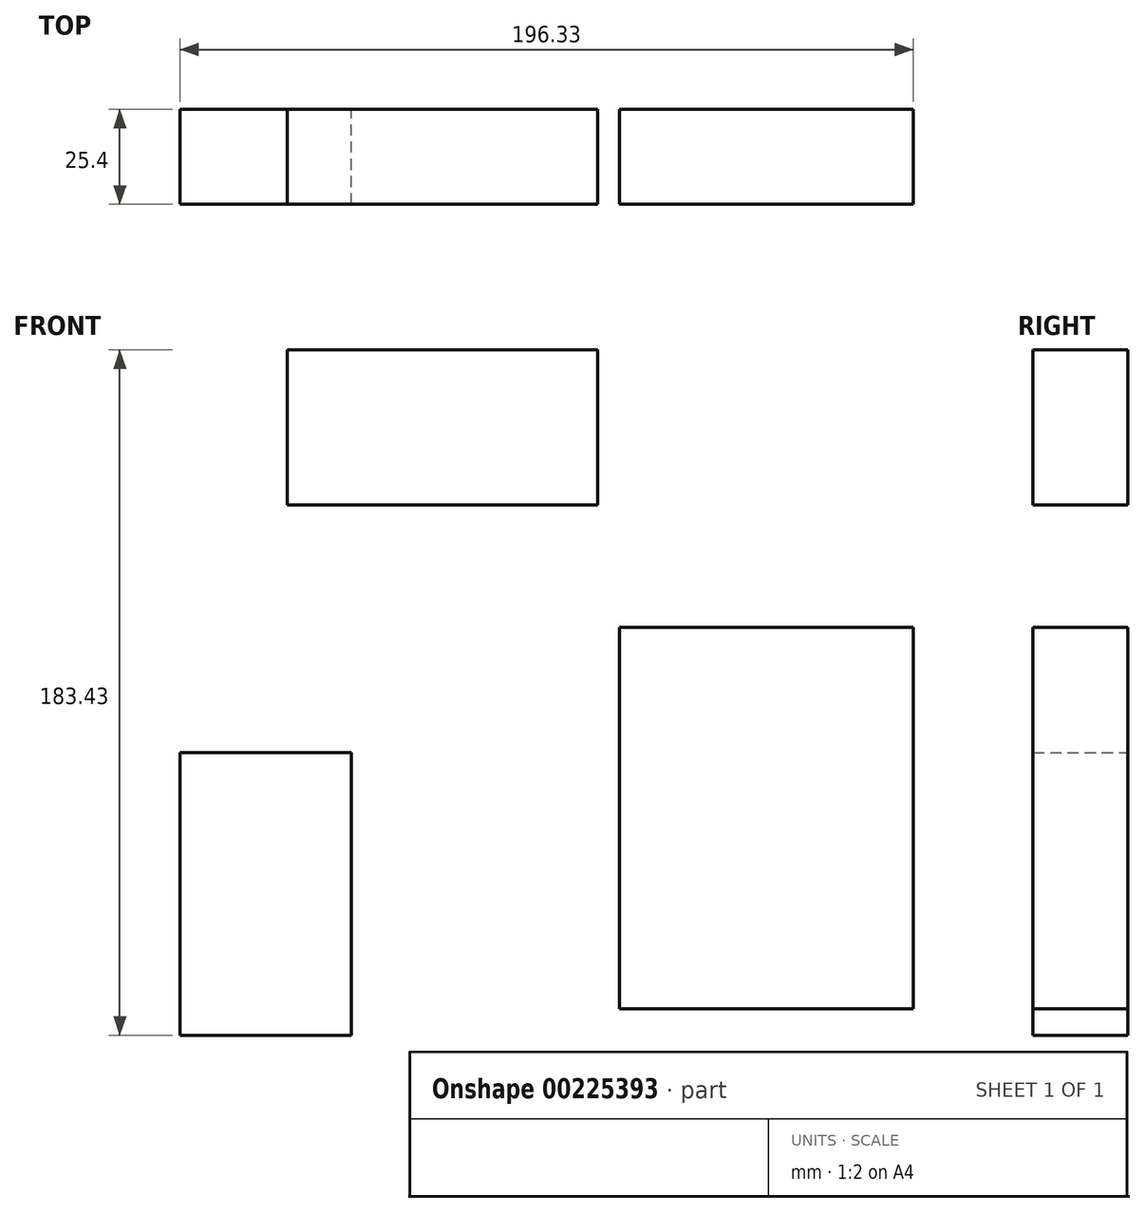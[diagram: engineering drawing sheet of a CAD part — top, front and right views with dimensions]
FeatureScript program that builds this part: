
annotation { "Feature Type Name" : "Feature", "Feature Type Description" : "" }
export const myFeature = defineFeature(function(context is Context, id is Id, definition is map)
    precondition{}
    {
        {
            var Q0;
            Q0=qCreatedBy(makeId("Front.planeOp"),FACE);
            var sketch = newSketch(context, id + "F1", { "sketchPlane" : qUnion([Q0])});
            skLineSegment(sketch, "E0.bottom", {"start": v(-68.37, 133.93) * mm, "end": v(14.6, 133.93) * mm});
            skLineSegment(sketch, "E0.top", {"start": v(-68.37, 92.48) * mm, "end": v(14.6, 92.48) * mm});
            skLineSegment(sketch, "E0.left", {"start": v(-68.37, 133.93) * mm, "end": v(-68.37, 92.48) * mm});
            skLineSegment(sketch, "E0.right", {"start": v(14.6, 133.93) * mm, "end": v(14.6, 92.48) * mm});
            skLineSegment(sketch, "E1.bottom", {"start": v(-97.16, 26.14) * mm, "end": v(-51.22, 26.14) * mm});
            skLineSegment(sketch, "E1.top", {"start": v(-97.16, -49.5) * mm, "end": v(-51.22, -49.5) * mm});
            skLineSegment(sketch, "E1.left", {"start": v(-97.16, 26.14) * mm, "end": v(-97.16, -49.5) * mm});
            skLineSegment(sketch, "E1.right", {"start": v(-51.22, 26.14) * mm, "end": v(-51.22, -49.5) * mm});
            skLineSegment(sketch, "E2.bottom", {"start": v(20.53, 59.7) * mm, "end": v(99.17, 59.7) * mm});
            skLineSegment(sketch, "E2.top", {"start": v(20.53, -42.39) * mm, "end": v(99.17, -42.39) * mm});
            skLineSegment(sketch, "E2.left", {"start": v(20.53, 59.7) * mm, "end": v(20.53, -42.39) * mm});
            skLineSegment(sketch, "E2.right", {"start": v(99.17, 59.7) * mm, "end": v(99.17, -42.39) * mm});
            skSolve(sketch);
        }
        {
            var Q0;
            Q0=qSketchRegion(id+"F1",true);
            extrude(context, id + "F2", {"entities" : qUnion([Q0]), "depth" : 25.4 * mm});
        }
    });
